# Revit family: Eurolan_Щеточный ввод
name_source: partatom
category: Устройства связи
units: mm (PartAtom-declared; Revit-internal decimal feet)

## family parameters
Всегда вертикально = Да
На основе рабочей плоскости = Нет
Общий = Нет
При загрузке вырезать с полостями = Нет
Размер круглого соединителя = Использовать диаметр
Сохранять ориентацию аннотаций = Нет
Тип детали = Нормальный
Точка расчета площади = Нет

## types (3) — shared parameters
ADSK_Единица измерения = шт
ADSK_Завод-изготовитель = Eurolan
ADSK_Количество = 1
ADSK_Материал = RAL9005
ADSK_Наименование краткое = Щеточный ввод

## per-type parameters (varying)
| type | ADSK_Код изделия | ADSK_Масса | ADSK_Наименование | Выбор_графики |
| Щеточный ввод_черный | 60A-35-10-30BL | 0.8 | Щеточный ввод, черный | Щеточный ввод_черный |
| Щеточный ввод 100 × 140 мм_черный | 60A-35-10-94BL | 0.5 | Щеточный ввод 100 × 140 мм, черный | Щеточный ввод 100 × 140 мм, черный |
| Щеточный ввод_серия N2000_черный | 60A-35-10-21BL | 0.09 | Щеточный ввод, серия N2000, черный | Щеточный ввод серия N2000 черный |
